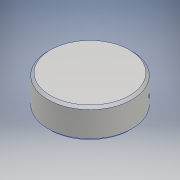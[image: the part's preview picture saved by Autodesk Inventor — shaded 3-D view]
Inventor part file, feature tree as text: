
AUTODESK INVENTOR PART (.ipt)
format: ipt  version: 2017 (Build 210142000, 142)  size: 147,968 bytes
history: native  units: mm
features: sketch x6, plane x4, hole x4, thread x4, extrude x1, chamfer x1
ambient origin geometry x8: Origin, YZ Plane, XZ Plane, XY Plane, X Axis, Y Axis, Z Axis, Center Point
bodies: Solid1 (feature_tree)
feature tree (20):
  extrude  "Extrusion1"  Depth=25.0mm TaperAngle=0.0deg
  chamfer  "Chamfer1"  Distance=2.0mm Angle=45.0deg
  sketch  "Sketch2"  dims[d6=6.981317mm d7=60.0deg]
  plane  "Work Plane1"
  plane  "Work Plane2"
  plane  "Work Plane3"
  plane  "Work Plane4"
  sketch  "Sketch3"  dims[d8=14.5mm d9=14.5mm]
  sketch  "Sketch4"  dims[d10=14.5mm d11=14.5mm]
  sketch  "Sketch5"  dims[d12=3.0mm d13=6.0mm d14=4.0mm d15=2.0mm d16=90.0deg d17=8.0mm d18=20.594885mm]
  hole  "Hole1"  [1 undecoded]
  hole  "Hole2"  [1 undecoded]
  hole  "Hole3"  [1 undecoded]
  hole  "Hole4"  [1 undecoded]
  thread  "Thread1"  [1 undecoded]
  thread  "Thread2"  [1 undecoded]
  thread  "Thread3"  [1 undecoded]
  thread  "Thread4"  [1 undecoded]
  sketch  "Sketch1"  dims[d0=70.0mm d1=25.0mm d2=0.0mm d3=2.0mm d4=2.0mm d5=45.0deg]
  sketch  "Sketch6"  dims[d19=3.0mm d20=6.0mm d21=4.0mm d22=2.0mm d23=90.0deg d24=8.0mm d25=20.594885mm d26=3.0mm d27=6.0mm d28=4.0mm d29=2.0mm d30=90.0deg d31=8.0mm d32=20.594885mm d33=3.0mm d34=6.0mm d35=4.0mm d36=2.0mm d37=90.0deg d38=8.0mm d39=20.594885mm d40=10.0mm d41=0.0mm d42=10.0mm d43=0.0mm d44=10.0mm d45=0.0mm d46=10.0mm d47=0.0mm d48=60.0deg]
note: 8 required parameter values undecoded (feature->parameter linkage not recoverable at this tier; creation-order binding heuristic only, values carry confidence <= 0.55)
